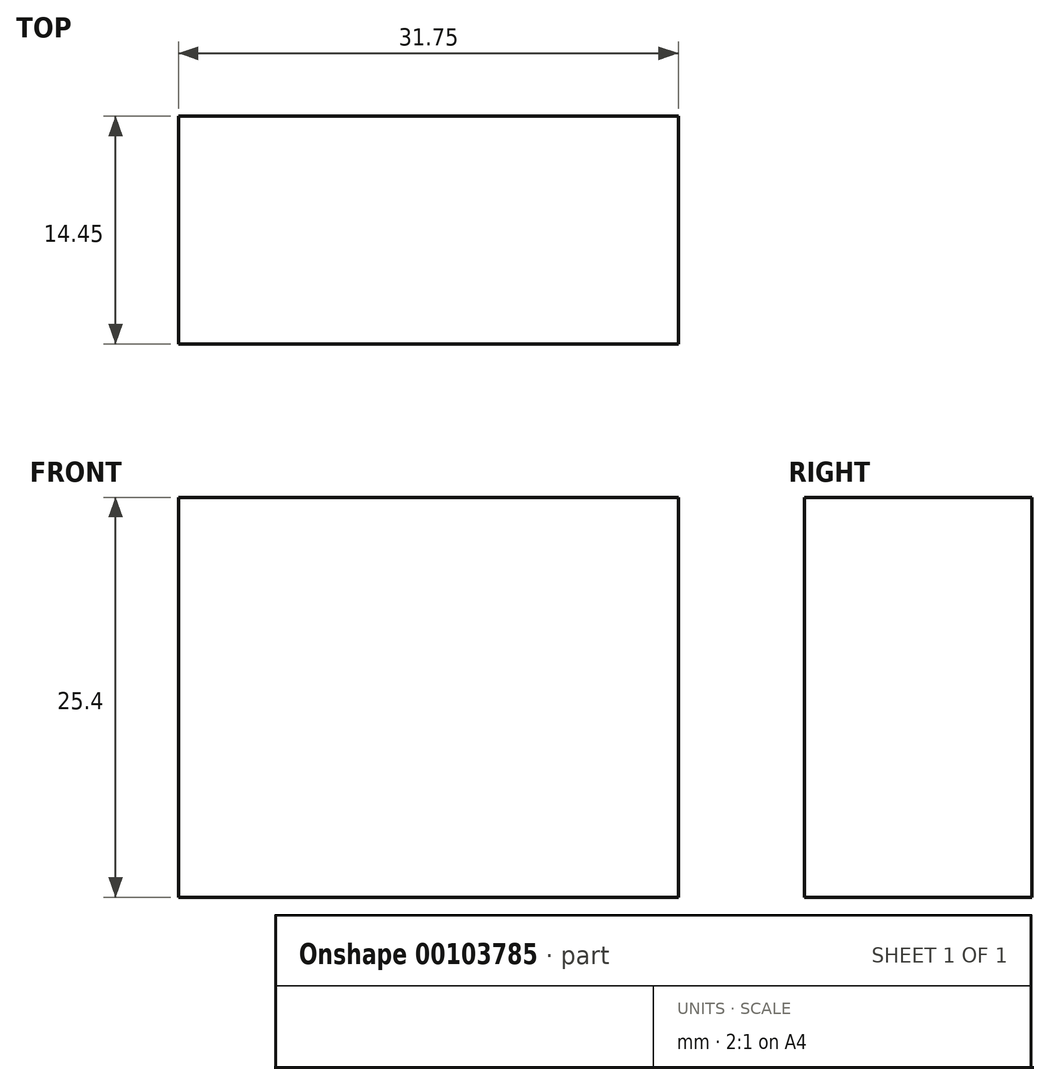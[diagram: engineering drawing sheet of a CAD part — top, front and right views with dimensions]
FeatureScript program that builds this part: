
annotation { "Feature Type Name" : "Feature", "Feature Type Description" : "" }
export const myFeature = defineFeature(function(context is Context, id is Id, definition is map)
    precondition{}
    {
        {
            var Q0;
            Q0=qCreatedBy(makeId("Front.planeOp"),FACE);
            var sketch = newSketch(context, id + "F0", { "sketchPlane" : qUnion([Q0])});
            skLineSegment(sketch, "E0.bottom", {"start": v(29.74, 12.7) * mm, "end": v(23.4, 12.7) * mm});
            skLineSegment(sketch, "E1.MirrorCS", {"start": v(29.74, -12.7) * mm, "end": v(23.4, -12.7) * mm});
            skLineSegment(sketch, "E2", {"start": v(23.4, 12.7) * mm, "end": v(-2, 12.7) * mm});
            skLineSegment(sketch, "E3", {"start": v(-2, 12.7) * mm, "end": v(-2, -12.7) * mm});
            skLineSegment(sketch, "E4", {"start": v(-2, -12.7) * mm, "end": v(23.4, -12.7) * mm});
            skLineSegment(sketch, "E5", {"start": v(29.74, 12.7) * mm, "end": v(29.74, -12.7) * mm});
            skPoint(sketch, "E6.end.orphan", {"position": v(29.74, 0) * mm});
            skPoint(sketch, "E0.right.end.orphan", {"position": v(23.4, 0) * mm});
            skLineSegment(sketch, "E7", {"start": v(-21.06, 131.2) * mm, "end": v(-21.06, -72) * mm});
            skPoint(sketch, "E8.MirrorCS.end.orphan", {"position": v(-40.1, 12.7) * mm});
            skPoint(sketch, "E8.MirrorCS.start.orphan", {"position": v(-65.5, 12.7) * mm});
            skPoint(sketch, "E9.MirrorCS.end.orphan", {"position": v(-40.1, -12.7) * mm});
            skPoint(sketch, "E10.MirrorCS.end.orphan", {"position": v(-65.5, -12.7) * mm});
            skPoint(sketch, "E11.MirrorCS.start.orphan", {"position": v(-71.86, -12.7) * mm});
            skPoint(sketch, "E12.MirrorCS.start.orphan", {"position": v(-71.86, 12.7) * mm});
            skPoint(sketch, "E13.end.orphan", {"position": v(55.14, 0) * mm});
            skSolve(sketch);
        }
        {
            var Q0;
            Q0=makeQuery(id+"F0.imprint","IMPRINT",FACE,{"disambiguationData":[TD([[makeQuery(id+"F0.imprint","IMPRINT",EDGE,{"derivedFrom":sQuery(id+"F0.wireOp",EDGE,"E0.bottom")}),1.0]])]});
            extrude(context, id + "F1", {"entities" : qUnion([Q0]), "depth" : 14.45 * mm});
        }
    });
